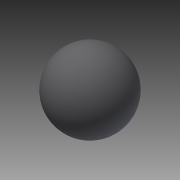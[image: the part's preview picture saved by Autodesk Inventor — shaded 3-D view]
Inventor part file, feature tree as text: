
AUTODESK INVENTOR PART (.ipt)
format: ipt  version: 2014 SP2 (Build 180246200, 246)  size: 112,640 bytes
history: native  units: mm
features: other x7, revolve x1, sketch x1
ambient origin geometry x8: Origin, YZ Plane, XZ Plane, XY Plane, X Axis, Y Axis, Z Axis, Center Point
bodies: Solid1 (feature_tree)
feature tree (9):
  revolve  "Revolution1"  [1 undecoded]
  other  "ip_st_1_XY"
  other  "ip_st_1_YZ"
  other  "ip_st_1_ZX"
  other  "ip_st_1_X"
  other  "ip_st_1_Y"
  other  "ip_st_1_Z"
  other  "ip_st_1_Center"
  sketch  "Sketch_1"  dims[d0=360.0deg]
note: 1 required parameter value undecoded (feature->parameter linkage not recoverable at this tier; creation-order binding heuristic only, values carry confidence <= 0.55)
